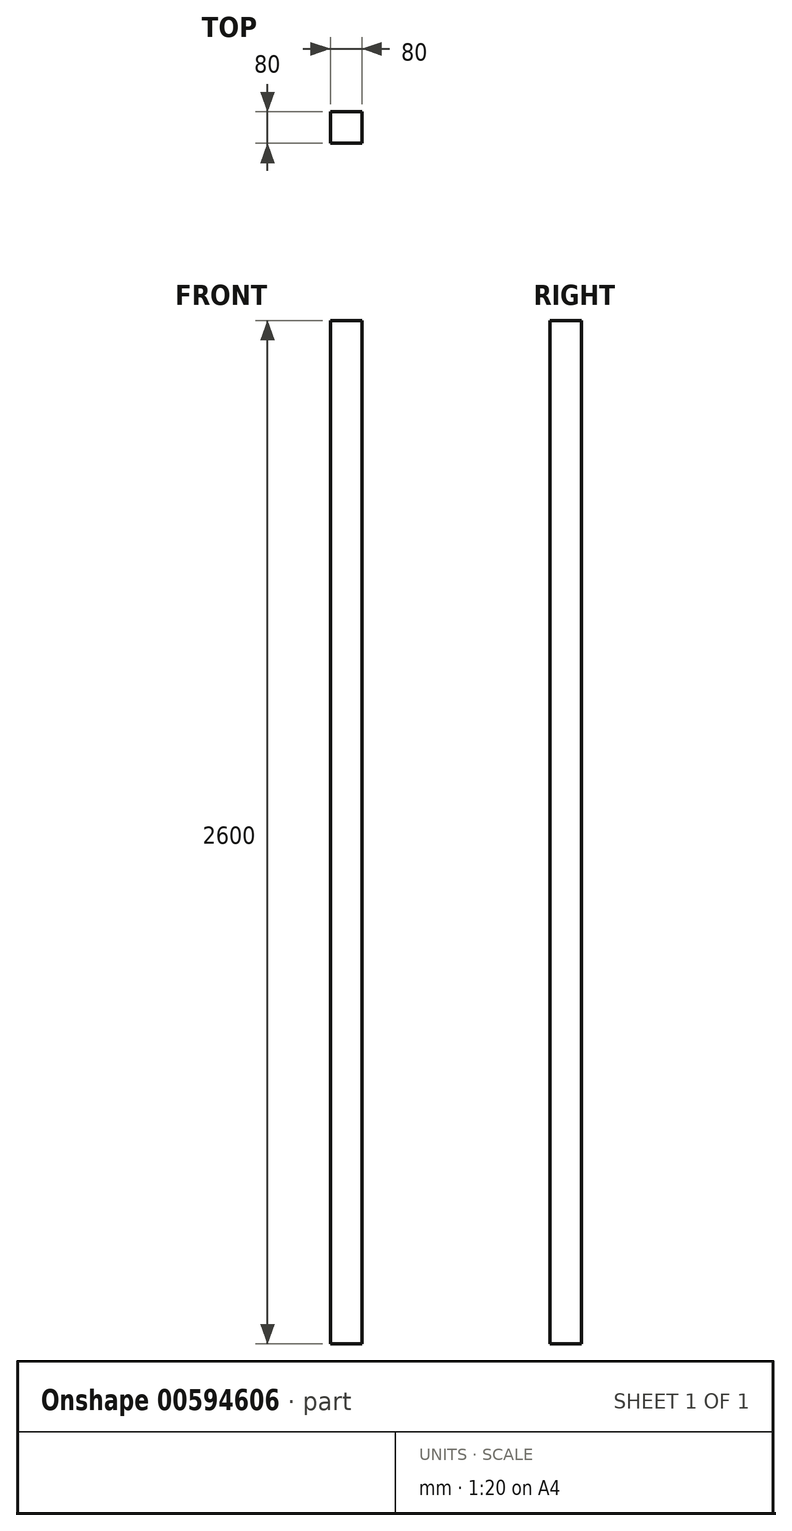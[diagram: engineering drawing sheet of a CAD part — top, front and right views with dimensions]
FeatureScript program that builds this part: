
annotation { "Feature Type Name" : "Feature", "Feature Type Description" : "" }
export const myFeature = defineFeature(function(context is Context, id is Id, definition is map)
    precondition{}
    {
        {
            var Q0;
            Q0=qCreatedBy(makeId("Top.planeOp"),FACE);
            var sketch = newSketch(context, id + "F0", { "sketchPlane" : qUnion([Q0])});
            skLineSegment(sketch, "E0.bottom", {"start": v(0, 0) * mm, "end": v(80, 0) * mm});
            skLineSegment(sketch, "E0.top", {"start": v(0, 80) * mm, "end": v(80, 80) * mm});
            skLineSegment(sketch, "E0.left", {"start": v(0, 0) * mm, "end": v(0, 80) * mm});
            skLineSegment(sketch, "E0.right", {"start": v(80, 0) * mm, "end": v(80, 80) * mm});
            skSolve(sketch);
        }
        {
            var Q0;
            Q0 = qSketchRegion(id + "F0", true);
            extrude(context, id + "F1", {"entities" : qUnion([Q0]), "depth" : 2600 * mm, "offsetDistance" : 25 * mm});
        }
    });
